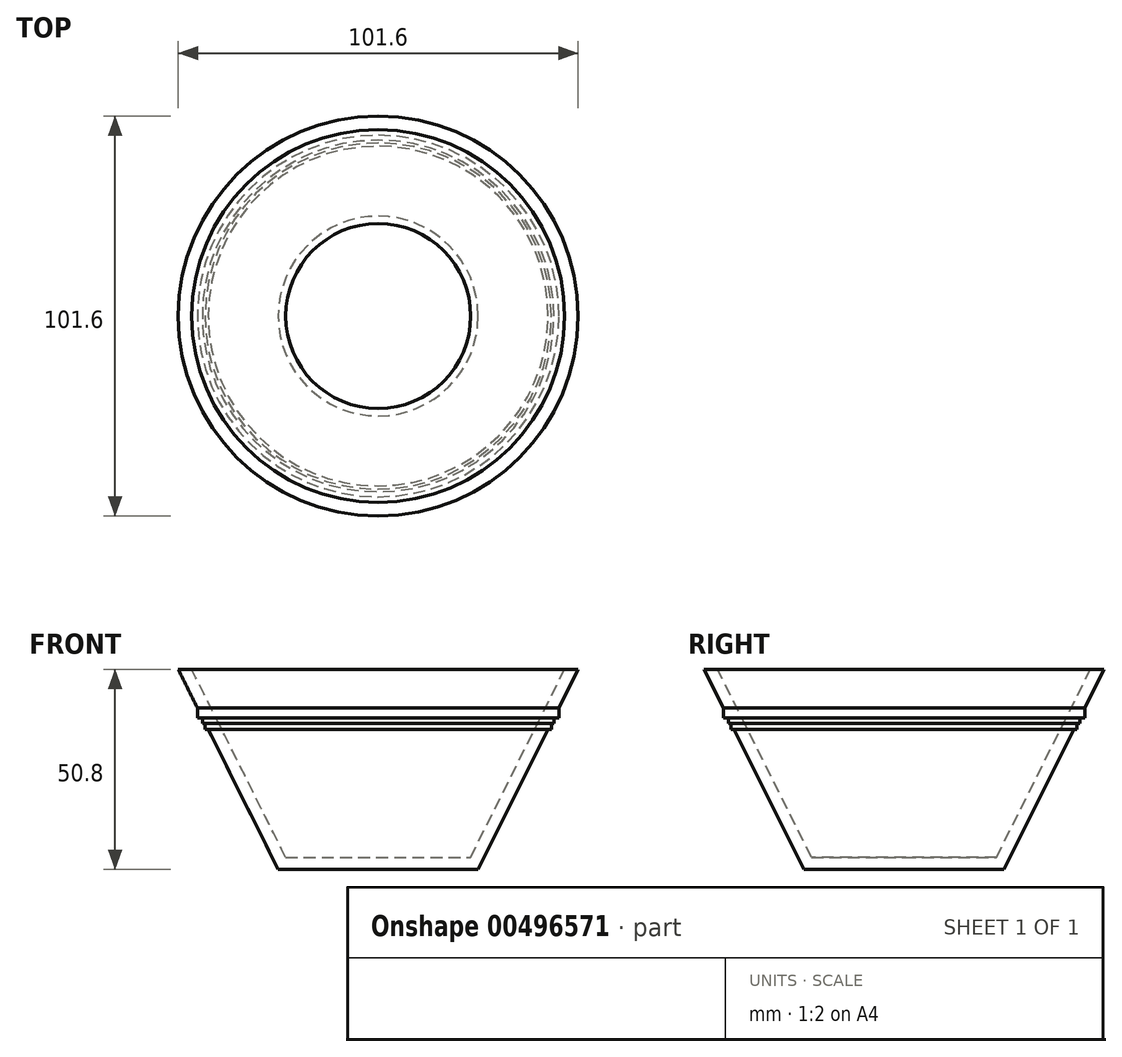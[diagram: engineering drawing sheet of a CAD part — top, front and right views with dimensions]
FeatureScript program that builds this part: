
annotation { "Feature Type Name" : "Feature", "Feature Type Description" : "" }
export const myFeature = defineFeature(function(context is Context, id is Id, definition is map)
    precondition{}
    {
        {
            var Q0;
            Q0=qCreatedBy(makeId("Front.planeOp"),FACE);
            var sketch = newSketch(context, id + "F0", { "sketchPlane" : qUnion([Q0])});
            skLineSegment(sketch, "E0", {"start": v(0, 0) * mm, "end": v(0, 50.8) * mm, "construction": true});
            skLineSegment(sketch, "E1", {"start": v(0, 0) * mm, "end": v(25.4, 0) * mm});
            skLineSegment(sketch, "E2", {"start": v(25.4, 0) * mm, "end": v(50.8, 50.8) * mm});
            skLineSegment(sketch, "E3.0", {"start": v(23.5, 3.07) * mm, "end": v(47.36, 50.8) * mm});
            skLineSegment(sketch, "E3.1", {"start": v(0, 3.07) * mm, "end": v(23.5, 3.07) * mm});
            skLineSegment(sketch, "E4", {"start": v(0, 3.07) * mm, "end": v(0, 0) * mm});
            skLineSegment(sketch, "E5", {"start": v(47.36, 50.8) * mm, "end": v(50.8, 50.8) * mm});
            skLineSegment(sketch, "E6", {"start": v(45.92, 41.04) * mm, "end": v(45.92, 38.52) * mm});
            skLineSegment(sketch, "E7", {"start": v(45.92, 38.52) * mm, "end": v(44.66, 38.52) * mm});
            skLineSegment(sketch, "E8", {"start": v(44.66, 38.52) * mm, "end": v(44.66, 37.14) * mm});
            skLineSegment(sketch, "E9", {"start": v(44.66, 37.14) * mm, "end": v(43.97, 37.14) * mm});
            skLineSegment(sketch, "E10", {"start": v(43.97, 37.14) * mm, "end": v(43.97, 35.52) * mm});
            skLineSegment(sketch, "E11", {"start": v(43.97, 35.52) * mm, "end": v(43.16, 35.52) * mm});
            skSolve(sketch);
        }
        {
            var Q0;
            Q0=makeQuery(id+"F0.imprint","IMPRINT",FACE,{"disambiguationData":[TD([[makeQuery(id+"F0.imprint","IMPRINT",EDGE,{"derivedFrom":sQuery(id+"F0.wireOp",EDGE,"E1")}),1.0]])]});
            var Q1;
            {var subQ0=sQuery(id+"F0.wireOp",EDGE,"E6");Q1=makeQuery(id+"F0.imprint","IMPRINT",FACE,{"disambiguationData":[TD([[makeQuery(id+"F0.imprint","IMPRINT",EDGE,{"derivedFrom":subQ0}),-1.0]])]});}
            var Q2;
            {var subQ0=sQuery(id+"F0.wireOp",EDGE,"E8");Q2=makeQuery(id+"F0.imprint","IMPRINT",FACE,{"disambiguationData":[TD([[makeQuery(id+"F0.imprint","IMPRINT",EDGE,{"derivedFrom":subQ0}),-1.0]])]});}
            var Q3;
            {var subQ0=sQuery(id+"F0.wireOp",EDGE,"E10");Q3=makeQuery(id+"F0.imprint","IMPRINT",FACE,{"disambiguationData":[TD([[makeQuery(id+"F0.imprint","IMPRINT",EDGE,{"derivedFrom":subQ0}),-1.0]])]});}
            var Q4;
            Q4=sQuery(id+"F0.wireOp",EDGE,"E0");
            revolve(context, id + "F1", {"entities" : qUnion([Q0, Q1, Q2, Q3]), "axis" : qUnion([Q4]), "revolveType" : RevolveType.FULL});
        }
    });
